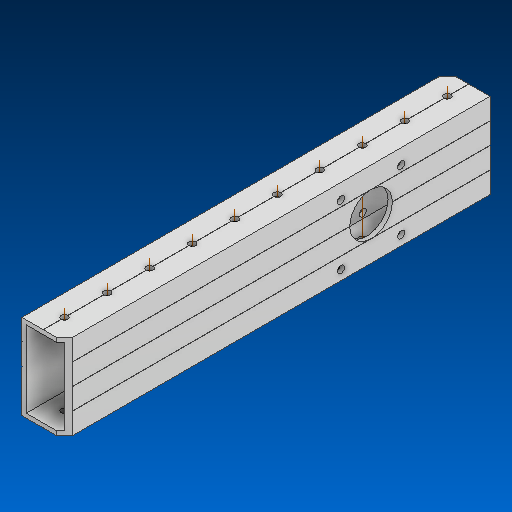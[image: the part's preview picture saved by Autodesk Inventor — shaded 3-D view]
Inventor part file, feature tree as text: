
AUTODESK INVENTOR PART (.ipt)
format: ipt  version: 2022.2 (Build 262287000, 287)  size: 547,840 bytes
history: native  units: in
note: dims shown in document units (in); Inventor stores cm internally (conversion verified against a paired STEP export)
features: other x16, extrude x3, sketch x3, pattern_linear x1, reference x1
ambient origin geometry x8: Origin, YZ Plane, XZ Plane, XY Plane, X Axis, Y Axis, Z Axis, Center Point
bodies: Solid1 (feature_tree)
feature tree (24):
  extrude  "Extrusion1"  Depth=2.0in
  other  "Work Axis1"
  pattern_linear  "Rectangular Pattern1"  Count1=10  [1 undecoded]
  extrude  "Extrusion2"  Depth=1.0in
  extrude  "Extrusion3"  TaperAngle=0.0deg  [1 undecoded]
  sketch  "Sketch1"  dims[d0=1.0in d1=2.0in]
  other  "Work Axis2"
  other  "Work Axis3"
  other  "Work Axis4"
  other  "Work Axis5"
  other  "Work Axis6"
  other  "Work Axis7"
  other  "Work Axis8"
  other  "Work Axis9"
  other  "Work Axis10"
  sketch  "Sketch2"  dims[d2=49.0in]
  sketch  "Sketch3"  dims[d3=0.0in d4=3.937in d6=1.0in d9=0.0in d10=0.0in d11=1.0in d12=0.0in d13=0.0in d14=0.17in d15=2.0in]
  reference  "Reference2"
  other  "Cut-Extrude2"
  parser-record x1  (decoder bookkeeping rows leaked as tree rows — omitted from the tree; the rows remain in map.json)
  other  "Chassis.iam"
  other  "VP Input to 2X Ring Gears to 90 Degree to VP Output:1"
  other  "Universal Female Output Shaft 1_2 Hex:1"
  other  "217-5839-006 Rev4_3"
note: 2 required parameter values undecoded (feature->parameter linkage not recoverable at this tier; creation-order binding heuristic only, values carry confidence <= 0.55)
note: 1 file-system path scrubbed to <path> (originals preserved in map.json)
